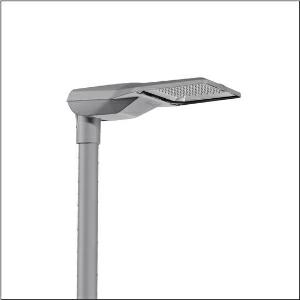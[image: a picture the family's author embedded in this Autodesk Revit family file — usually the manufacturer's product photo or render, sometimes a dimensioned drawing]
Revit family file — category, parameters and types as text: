
# Revit family: streetlight_sl_21_midi___st1_0a_5xe7d63a08lb_3853
name_source: partatom
category: Lighting Fixtures
units: mm (PartAtom-declared; Revit-internal decimal feet)

## family parameters
Cut with Voids When Loaded = No
Host = Face
Light Source = No
Part Type = Normal
Room Calculation Point = No
Round Connector Dimension = Use Diameter
Shared = No

## types (1)
- --- (1 x LED, 12860 lm, 98.3 W, 2700K)
    Apparent Load = 98 VA
    CIE Flux Codes = 37 72 97 100 100
    Color Rendering = 70
    Color Temperature = 2700K
    Default Elevation = 1800 mm
    Description = Streetlight SL 21 midi, mast luminaire, primary light control with lens, of PMMA, primary optical cover: cover, of toughened safety glass, transparent, light distribution: ST1.0a, light emission: direct distribution, primary light characteristic: asymmetric, installation type: post-top, side-entry, LED, 3G 1.5mm², High Power LED, rated luminous flux: 12.860lm, luminous efficacy: 131lm/W, light colour: 727, colour temperature: 2700K, control: overheat protection, constant luminous flux control, time-dependent luminous flux control, flexible luminous flux parameterisation, mains connection: 220..240V, AC, 50/60Hz, connection cable pre-assembled, cable length: 10,5m, wiring characteristics: H07RN-F, start of lifetime: 98W, end of service life: 101W, reduction: 44W, luminaire housing, of diecast aluminium, powder-coated, Siteco® metallic grey (DB 702S), corrosivity category C5 mid according to DIN EN ISO 12944, please order mast flange separately, inclination adjustable: 0°, 5°, 10°, 15°, sealing non-destructively replaceable, multi-level sealing system, length: 644mm, width: 335mm, height: 110mm, mast flange for spigot size: 42mm (side-entry): 5XC10008XM4, 60/48mm (side-entry/post-top): 5XC10108XM2, 76/60mm (side-entry/post-top): 5XC10108XM1, protection rating (complete): IP66, insulation class (complete): insulation class II (safety insulation), certification: CE, ENEC, ENEC+, VDE, impact resistance: IK09, permissible operating ambient temperature for outdoor applications: -40..+50°C, standard-compliant lighting for roads and squares, packaging unit: 1 piece

Light Distribution: ST1.0a
    Height = 111 mm
    Lamp = 1 x LED
    Lamp Light Flux = 12860 lm
    Lamp Power = 98.3 W
    Lamp count = 1
    Length = 644 mm
    Luminous efficacy = 131 lm/W
    Manufacturer = Siteco
    ModVariant = No
    Model = 5XE7D63A08LB
    Number of Poles = 1
    OnlyDefault = Yes
    Power Factor = 1
    Product Name = Streetlight SL 21 midi | ST1.0a
    Product group = mast luminaire | pylon top
    ProductGroupID = 6100
    Protection Class = Protection class II
    Protection Degree = IP 66
    RLX_Detail_Level = 1
    RLX_Emergency_Light_Flux = 0 lm
    RLX_Emergency_Type = 0
    RLX_Emergency_Type_DB = No
    RlxData = <blob elided: 90673 chars, md5=90143d1a>
    Socket = socket
    Standby Power = 0 W
    System Light Flux = 12860 lm
    System Power = 98 W
    Type Comments = factory setting: luminous flux: 100 % | Output Level: 100 % | 1020 mA
    Type Image = l_1004298.jpg
    URL = http://relux.com
    VarID = @adj_141127
    Voltage = 0 V
    Weight = 0.00 kg
    Width = 336 mm

## geometry (parser evidence)
native form markers: Blend x4, Sweep x10
no freeform markers — native parametric forms only
